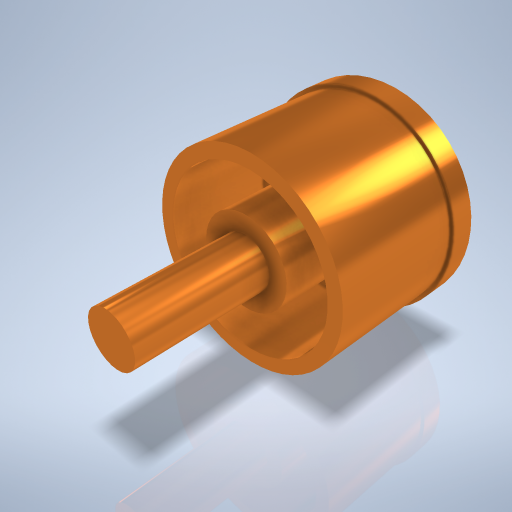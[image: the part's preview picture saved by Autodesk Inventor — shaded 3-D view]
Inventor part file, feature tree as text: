
AUTODESK INVENTOR PART (.ipt)
format: ipt  version: 2024.2 (Build 282272000, 272)  size: 345,088 bytes
history: native  units: mm
features: sketch x8, extrude x5, hole x2, plane x1, revolve x1
ambient origin geometry x8: Origin, YZ Plane, XZ Plane, XY Plane, X Axis, Y Axis, Z Axis, Center Point
bodies: Volumenkörper1 (feature_tree)
feature tree (17):
  extrude  "Extrusion1"  Depth=3.0mm TaperAngle=0.0deg
  extrude  "Extrusion2"  Depth=16.0mm TaperAngle=0.0deg
  extrude  "Extrusion5"  Depth=13.0mm TaperAngle=0.0deg
  extrude  "Extrusion6"  Depth=13.0mm TaperAngle=0.0deg
  extrude  "Extrusion7"  Depth=16.0mm TaperAngle=0.0deg
  hole  "Bohrung2"  [1 undecoded]
  plane  "Arbeitsebene3"
  revolve  "Umdrehung1"
  hole  "Bohrung4"  [1 undecoded]
  sketch  "Skizze1"  dims[d0=25.5mm d1=3.0mm d2=0.0mm]
  sketch  "Skizze2"  dims[d3=24.5mm d4=16.0mm d5=0.0mm]
  sketch  "Skizze6"  dims[d20=21.0mm d21=13.0mm d22=0.0mm]
  sketch  "Skizze7"  dims[d23=11.0mm d24=13.0mm d25=0.0mm]
  sketch  "Skizze8"  dims[d26=6.5mm d27=16.0mm d28=0.0mm]
  sketch  "Skizze9"  dims[d29=5.0mm d30=6.0mm d31=4.0mm d32=2.0mm d33=90.0deg d34=15.8mm d35=0.0mm d37=0.0mm]
  sketch  "Skizze11"  dims[d38=3.0mm d39=4.0mm]
  sketch  "Skizze14"  dims[d40=9.5mm d41=6.5mm d42=360.0deg d50=4.0mm d51=6.0mm d52=4.0mm d53=2.0mm d54=90.0deg d55=5.0mm d56=0.0mm]
note: 2 required parameter values undecoded (feature->parameter linkage not recoverable at this tier; creation-order binding heuristic only, values carry confidence <= 0.55)
